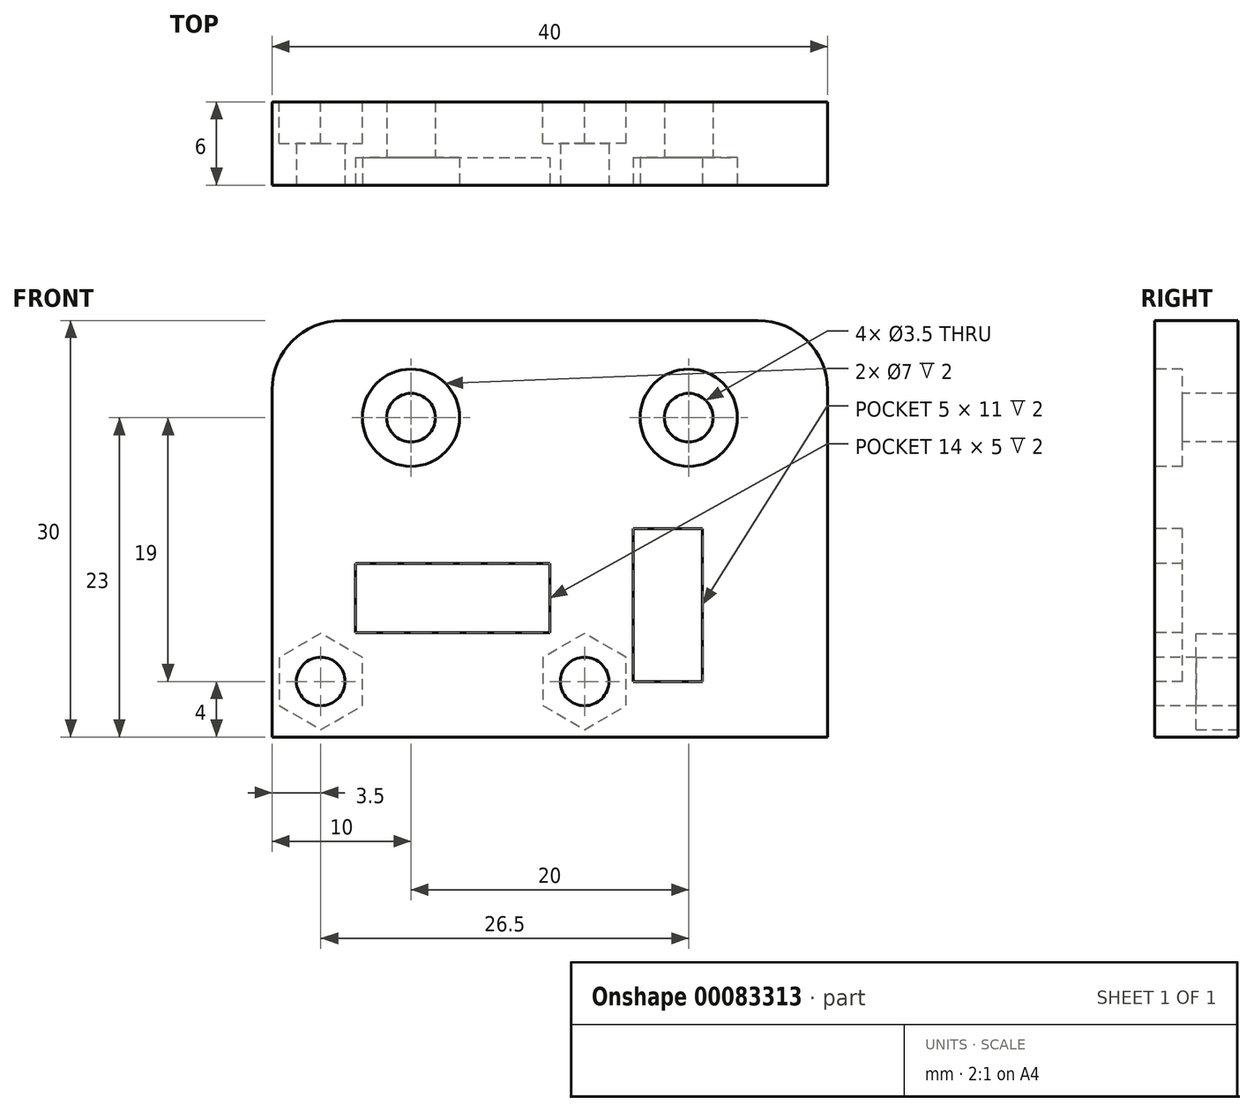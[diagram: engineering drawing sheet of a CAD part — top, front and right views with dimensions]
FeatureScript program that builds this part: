
annotation { "Feature Type Name" : "Feature", "Feature Type Description" : "" }
export const myFeature = defineFeature(function(context is Context, id is Id, definition is map)
    precondition{}
    {
        {
            var Q0;
            Q0=qCreatedBy(makeId("Front.planeOp"),FACE);
            var sketch = newSketch(context, id + "F0", { "sketchPlane" : qUnion([Q0])});
            skLineSegment(sketch, "E0.bottom", {"start": v(20, 15) * mm, "end": v(-20, 15) * mm});
            skLineSegment(sketch, "E0.top", {"start": v(20, -15) * mm, "end": v(-20, -15) * mm});
            skLineSegment(sketch, "E0.left", {"start": v(20, 15) * mm, "end": v(20, -15) * mm});
            skLineSegment(sketch, "E0.right", {"start": v(-20, 15) * mm, "end": v(-20, -15) * mm});
            skPoint(sketch, "E0.middle", {"position": v(0, 0) * mm});
            skLineSegment(sketch, "E1", {"start": v(-20, -13.5) * mm, "end": v(20, -13.5) * mm, "construction": true});
            skLineSegment(sketch, "E2", {"start": v(-20, -11) * mm, "end": v(20, -11) * mm, "construction": true});
            skLineSegment(sketch, "E3", {"start": v(-20, 8) * mm, "end": v(20, 8) * mm, "construction": true});
            skCircle(sketch, "E4", {"center": v(-16.5, -11) * mm, "radius": 1.75 * mm});
            skCircle(sketch, "E5", {"center": v(2.5, -11) * mm, "radius": 1.75 * mm});
            skLineSegment(sketch, "E6.bottom", {"start": v(6, -11) * mm, "end": v(11, -11) * mm});
            skLineSegment(sketch, "E6.top", {"start": v(6, 0) * mm, "end": v(11, 0) * mm});
            skLineSegment(sketch, "E6.left", {"start": v(6, -11) * mm, "end": v(6, 0) * mm});
            skLineSegment(sketch, "E6.right", {"start": v(11, -11) * mm, "end": v(11, 0) * mm});
            skLineSegment(sketch, "E7.bottom", {"start": v(-14, -7.5) * mm, "end": v(0, -7.5) * mm});
            skLineSegment(sketch, "E7.top", {"start": v(-14, -2.5) * mm, "end": v(0, -2.5) * mm});
            skLineSegment(sketch, "E7.left", {"start": v(-14, -7.5) * mm, "end": v(-14, -2.5) * mm});
            skLineSegment(sketch, "E7.right", {"start": v(0, -7.5) * mm, "end": v(0, -2.5) * mm});
            skLineSegment(sketch, "E8", {"start": v(0, 20.68) * mm, "end": v(0, -38.74) * mm, "construction": true});
            skCircle(sketch, "E9", {"center": v(-10, 8) * mm, "radius": 1.75 * mm});
            skCircle(sketch, "E10", {"center": v(10, 8) * mm, "radius": 1.75 * mm});
            skCircle(sketch, "E11", {"center": v(-10, 8) * mm, "radius": 3.5 * mm});
            skCircle(sketch, "E12", {"center": v(10, 8) * mm, "radius": 3.5 * mm});
            skSolve(sketch);
        }
        {
            var Q0;
            Q0=makeQuery(id+"F0.imprint","IMPRINT",FACE,{"disambiguationData":[TD([[makeQuery(id+"F0.imprint","IMPRINT",EDGE,{"derivedFrom":sQuery(id+"F0.wireOp",EDGE,"E0.bottom")}),1.0]])]});
            var Q1;
            Q1=makeQuery(id+"F0.imprint","IMPRINT",FACE,{"disambiguationData":[TD([[makeQuery(id+"F0.imprint","IMPRINT",EDGE,{"derivedFrom":sQuery(id+"F0.wireOp",EDGE,"E7.bottom")}),1.0]])]});
            var Q2;
            Q2=makeQuery(id+"F0.imprint","IMPRINT",FACE,{"disambiguationData":[TD([[makeQuery(id+"F0.imprint","IMPRINT",EDGE,{"derivedFrom":sQuery(id+"F0.wireOp",EDGE,"E6.bottom")}),1.0]])]});
            var Q3;
            Q3=makeQuery(id+"F0.imprint","IMPRINT",FACE,{"disambiguationData":[TD([[makeQuery(id+"F0.imprint","IMPRINT",EDGE,{"derivedFrom":sQuery(id+"F0.wireOp",EDGE,"E10")}),-1.0]])]});
            var Q4;
            Q4=makeQuery(id+"F0.imprint","IMPRINT",FACE,{"disambiguationData":[TD([[makeQuery(id+"F0.imprint","IMPRINT",EDGE,{"derivedFrom":sQuery(id+"F0.wireOp",EDGE,"E9")}),-1.0]])]});
            extrude(context, id + "F1", {"entities" : qUnion([Q0, Q1, Q2, Q3, Q4]), "oppositeDirection" : true, "depth" : 6 * mm});
        }
        {
            var Q0;
            Q0=makeQuery(id+"F0.imprint","IMPRINT",FACE,{"disambiguationData":[TD([[makeQuery(id+"F0.imprint","IMPRINT",EDGE,{"derivedFrom":sQuery(id+"F0.wireOp",EDGE,"E6.bottom")}),1.0]])]});
            var Q1;
            Q1=makeQuery(id+"F0.imprint","IMPRINT",FACE,{"disambiguationData":[TD([[makeQuery(id+"F0.imprint","IMPRINT",EDGE,{"derivedFrom":sQuery(id+"F0.wireOp",EDGE,"E7.bottom")}),1.0]])]});
            var Q2;
            Q2=makeQuery(id+"F0.imprint","IMPRINT",FACE,{"disambiguationData":[TD([[makeQuery(id+"F0.imprint","IMPRINT",EDGE,{"derivedFrom":sQuery(id+"F0.wireOp",EDGE,"E9")}),-1.0]])]});
            var Q3;
            Q3=makeQuery(id+"F0.imprint","IMPRINT",FACE,{"disambiguationData":[TD([[makeQuery(id+"F0.imprint","IMPRINT",EDGE,{"derivedFrom":sQuery(id+"F0.wireOp",EDGE,"E10")}),-1.0]])]});
            extrude(context, id + "F2", {"entities" : qUnion([Q0, Q1, Q2, Q3]), "operationType" : NewBodyOperationType.REMOVE, "oppositeDirection" : true, "depth" : 2 * mm});
        }
        {
            var Q0;
            Q0=makeQuery(id+"F1.opExtrude","CAP_FACE",FACE,{"disambiguationData":[OSD([sQuery(id+"F0.wireOp",EDGE,"E0.bottom"),sQuery(id+"F0.wireOp",EDGE,"E0.top"),sQuery(id+"F0.wireOp",EDGE,"E0.left"),sQuery(id+"F0.wireOp",EDGE,"E0.right"),sQuery(id+"F0.wireOp",EDGE,"E4"),sQuery(id+"F0.wireOp",EDGE,"E5"),sQuery(id+"F0.wireOp",EDGE,"E9"),sQuery(id+"F0.wireOp",EDGE,"E10")])],"isStart":false});
            var sketch = newSketch(context, id + "F3", { "sketchPlane" : qUnion([Q0])});
            skCircle(sketch, "E13.cCircle", {"center": v(-2.5, -11) * mm, "radius": 3 * mm, "construction": true});
            skLineSegment(sketch, "E13.0", {"start": v(-5.5, -9.27) * mm, "end": v(-2.5, -7.54) * mm});
            skLineSegment(sketch, "E13.1", {"start": v(-2.5, -7.54) * mm, "end": v(0.5, -9.27) * mm});
            skLineSegment(sketch, "E13.2", {"start": v(0.5, -9.27) * mm, "end": v(0.5, -12.73) * mm});
            skLineSegment(sketch, "E13.3", {"start": v(0.5, -12.73) * mm, "end": v(-2.5, -14.46) * mm});
            skLineSegment(sketch, "E13.4", {"start": v(-2.5, -14.46) * mm, "end": v(-5.5, -12.73) * mm});
            skLineSegment(sketch, "E13.5", {"start": v(-5.5, -12.73) * mm, "end": v(-5.5, -9.27) * mm});
            skPoint(sketch, "E13.0.midPoint", {"position": v(-4, -8.4) * mm});
            skCircle(sketch, "E14.cCircle", {"center": v(16.5, -11) * mm, "radius": 3 * mm, "construction": true});
            skLineSegment(sketch, "E14.0", {"start": v(13.5, -12.73) * mm, "end": v(13.5, -9.27) * mm});
            skLineSegment(sketch, "E14.1", {"start": v(13.5, -9.27) * mm, "end": v(16.5, -7.54) * mm});
            skLineSegment(sketch, "E14.2", {"start": v(16.5, -7.54) * mm, "end": v(19.5, -9.27) * mm});
            skLineSegment(sketch, "E14.3", {"start": v(19.5, -9.27) * mm, "end": v(19.5, -12.73) * mm});
            skLineSegment(sketch, "E14.4", {"start": v(19.5, -12.73) * mm, "end": v(16.5, -14.46) * mm});
            skLineSegment(sketch, "E14.5", {"start": v(16.5, -14.46) * mm, "end": v(13.5, -12.73) * mm});
            skPoint(sketch, "E14.0.midPoint", {"position": v(13.5, -11) * mm});
            skSolve(sketch);
        }
        {
            var Q0;
            Q0 = qSketchRegion(id + "F3", true);
            extrude(context, id + "F4", {"entities" : qUnion([Q0]), "operationType" : NewBodyOperationType.REMOVE, "oppositeDirection" : true, "depth" : 3 * mm});
        }
        {
            var Q0;
            Q0=makeQuery(id+"F1.opExtrude","SWEPT_EDGE",EDGE,{"disambiguationData":[OSD([sQuery(id+"F0.wireOp",EDGE,"E0.bottom"),sQuery(id+"F0.wireOp",EDGE,"E0.left")])]});
            var Q1;
            Q1=makeQuery(id+"F1.opExtrude","SWEPT_EDGE",EDGE,{"disambiguationData":[OSD([sQuery(id+"F0.wireOp",EDGE,"E0.bottom"),sQuery(id+"F0.wireOp",EDGE,"E0.right")])]});
            fillet(context, id + "F5", {"entities" : qUnion([Q0, Q1]), "radius" : 5 * mm, "tangentPropagation" : true, "allowEdgeOverflow" : false});
        }
    });
